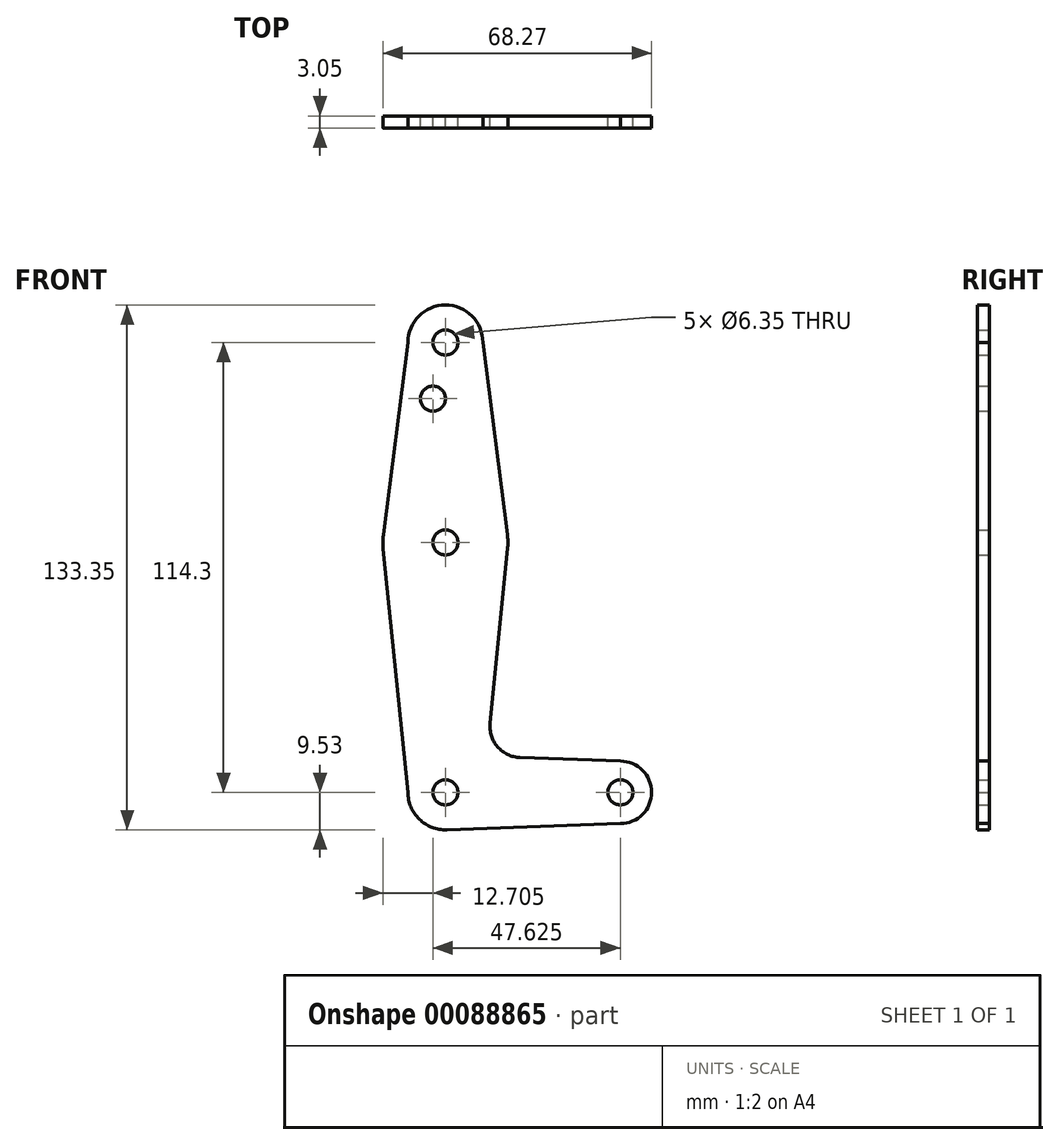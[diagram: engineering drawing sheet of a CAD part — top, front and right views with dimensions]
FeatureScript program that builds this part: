
annotation { "Feature Type Name" : "Feature", "Feature Type Description" : "" }
export const myFeature = defineFeature(function(context is Context, id is Id, definition is map)
    precondition{}
    {
        {
            var Q0;
            Q0=qCreatedBy(makeId("Front.planeOp"),FACE);
            var sketch = newSketch(context, id + "F0", { "sketchPlane" : qUnion([Q0])});
            skCircle(sketch, "E0", {"center": v(0, 50.8) * mm, "radius": 9.53 * mm});
            skLineSegment(sketch, "E1", {"start": v(0, 50.8) * mm, "end": v(0, 0) * mm, "construction": true});
            skCircle(sketch, "E2", {"center": v(0, 0) * mm, "radius": 15.88 * mm});
            skLineSegment(sketch, "E3", {"start": v(0, 0) * mm, "end": v(0, -63.5) * mm, "construction": true});
            skCircle(sketch, "E4", {"center": v(0, -63.5) * mm, "radius": 9.53 * mm});
            skLineSegment(sketch, "E5", {"start": v(0, -63.5) * mm, "end": v(44.45, -63.5) * mm});
            skCircle(sketch, "E6", {"center": v(44.45, -63.5) * mm, "radius": 7.94 * mm});
            skLineSegment(sketch, "E7", {"start": v(44.45, -71.44) * mm, "end": v(0, -73.03) * mm});
            skLineSegment(sketch, "E8", {"start": v(-9.53, 50.8) * mm, "end": v(-15.75, 2) * mm});
            skLineSegment(sketch, "E9", {"start": v(9.52, 50.8) * mm, "end": v(15.75, 2) * mm});
            skLineSegment(sketch, "E10", {"start": v(-9.52, -63.5) * mm, "end": v(-15.8, -1.6) * mm});
            skCircle(sketch, "E11", {"center": v(-3.18, 36.53) * mm, "radius": 3.18 * mm});
            skPoint(sketch, "E12.newPointB", {"position": v(0, -53.97) * mm});
            skCircle(sketch, "E13", {"center": v(0, 50.8) * mm, "radius": 3.18 * mm});
            skCircle(sketch, "E14", {"center": v(0, 0) * mm, "radius": 3.18 * mm});
            skCircle(sketch, "E15", {"center": v(0, -63.5) * mm, "radius": 3.18 * mm});
            skCircle(sketch, "E16", {"center": v(44.45, -63.5) * mm, "radius": 3.18 * mm});
            skLineSegment(sketch, "E17", {"start": v(44.45, -55.56) * mm, "end": v(18.97, -54.65) * mm});
            skLineSegment(sketch, "E18", {"start": v(11.34, -45.9) * mm, "end": v(15.8, -1.59) * mm});
            skArc(sketch, "E19.filletArc", {"start": v(11.34, -45.9) * mm, "mid": v(13.26, -51.93) * mm, "end": v(18.97, -54.65) * mm});
            skSolve(sketch);
        }
        {
            var Q0;
            Q0 = qSketchRegion(id + "F0", true);
            extrude(context, id + "F1", {"entities" : qUnion([Q0]), "depth" : 3.05 * mm});
        }
        {
            var Q0;
            Q0 = qSketchRegion(id + "F0", true);
            extrude(context, id + "F2", {"entities" : qUnion([Q0]), "operationType" : NewBodyOperationType.ADD, "depth" : 3.05 * mm});
        }
    });
